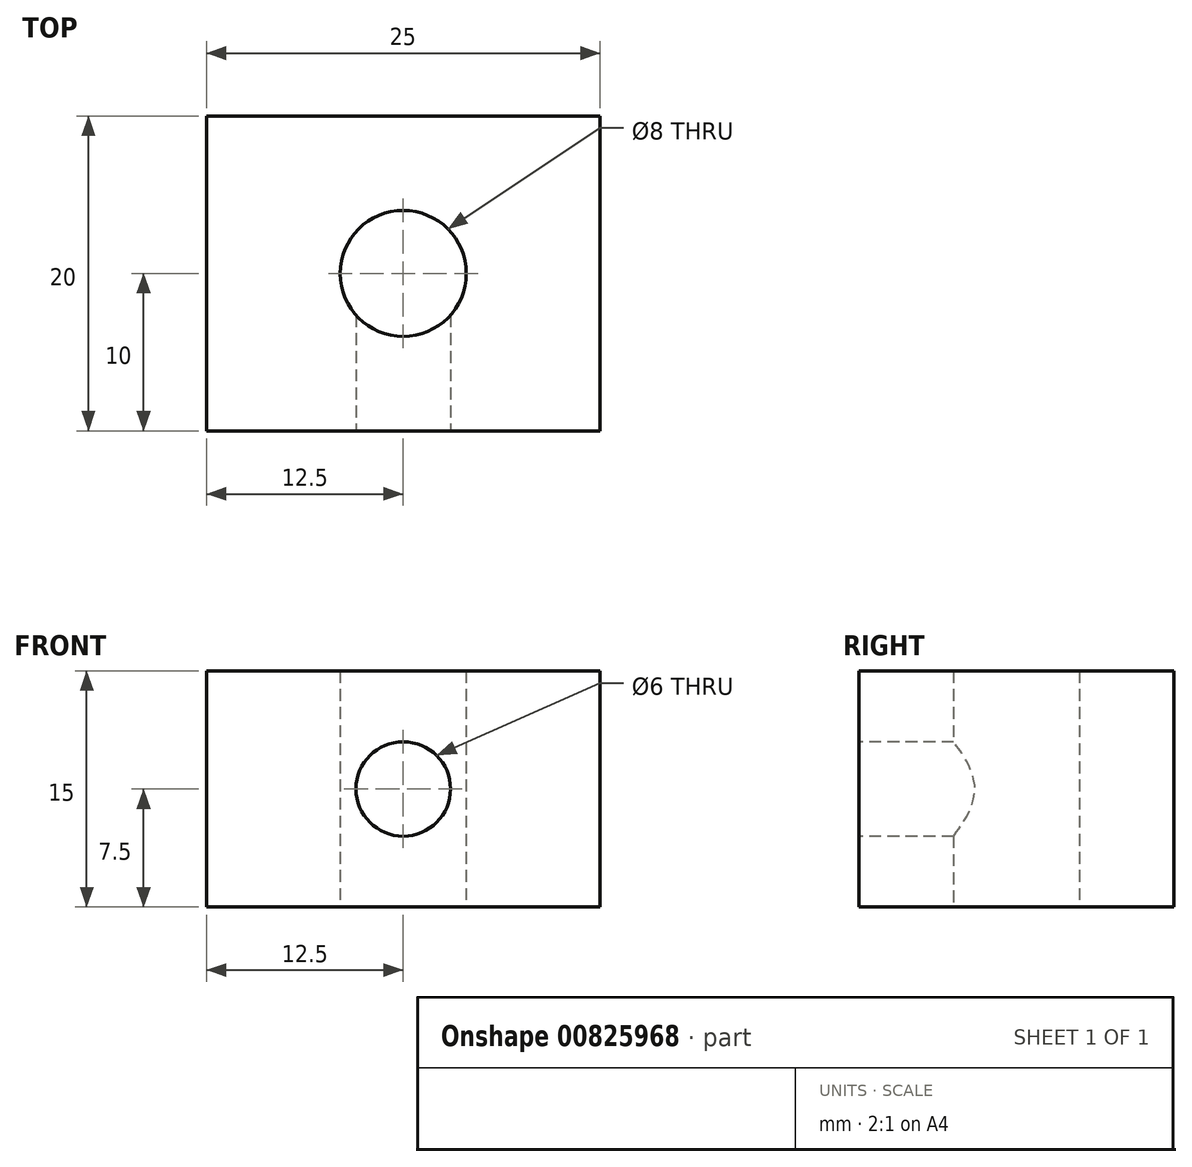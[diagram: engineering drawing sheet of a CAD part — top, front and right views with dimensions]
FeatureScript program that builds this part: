
annotation { "Feature Type Name" : "Feature", "Feature Type Description" : "" }
export const myFeature = defineFeature(function(context is Context, id is Id, definition is map)
    precondition{}
    {
        {
            var Q0;
            Q0=qCreatedBy(makeId("Top.planeOp"),FACE);
            var sketch = newSketch(context, id + "F0", { "sketchPlane" : qUnion([Q0])});
            skLineSegment(sketch, "E0.bottom", {"start": v(0, 0) * mm, "end": v(25, 0) * mm});
            skLineSegment(sketch, "E0.top", {"start": v(0, -20) * mm, "end": v(25, -20) * mm});
            skLineSegment(sketch, "E0.left", {"start": v(0, 0) * mm, "end": v(0, -20) * mm});
            skLineSegment(sketch, "E0.right", {"start": v(25, 0) * mm, "end": v(25, -20) * mm});
            skCircle(sketch, "E1", {"center": v(12.5, -10) * mm, "radius": 4 * mm});
            skLineSegment(sketch, "E2", {"start": v(0, -10) * mm, "end": v(12.5, -10) * mm, "construction": true});
            skLineSegment(sketch, "E3", {"start": v(12.5, -20) * mm, "end": v(12.5, -10) * mm, "construction": true});
            skSolve(sketch);
        }
        {
            var Q0;
            Q0=makeQuery(id+"F0.imprint","IMPRINT",FACE,{"disambiguationData":[TD([[makeQuery(id+"F0.imprint","IMPRINT",EDGE,{"derivedFrom":sQuery(id+"F0.wireOp",EDGE,"E0.bottom")}),-1.0]])]});
            extrude(context, id + "F1", {"entities" : qUnion([Q0]), "depth" : 15 * mm, "offsetDistance" : 25.4 * mm});
        }
        {
            var Q0;
            Q0=makeQuery(id+"F1.opExtrude","SWEPT_FACE",FACE,{"disambiguationData":[OSD([sQuery(id+"F0.wireOp",EDGE,"E0.top")])]});
            var sketch = newSketch(context, id + "F2", { "sketchPlane" : qUnion([Q0])});
            skCircle(sketch, "E4", {"center": v(12.5, 7.5) * mm, "radius": 3 * mm});
            skLineSegment(sketch, "E5", {"start": v(0, 7.5) * mm, "end": v(12.5, 7.5) * mm, "construction": true});
            skLineSegment(sketch, "E6", {"start": v(12.5, 0) * mm, "end": v(12.5, 7.5) * mm, "construction": true});
            skSolve(sketch);
        }
        {
            var Q0;
            Q0=makeQuery(id+"F2.imprint","IMPRINT",FACE,{"disambiguationData":[TD([[makeQuery(id+"F2.imprint","IMPRINT",EDGE,{"derivedFrom":sQuery(id+"F2.wireOp",EDGE,"E4")}),1.0]])]});
            extrude(context, id + "F3", {"entities" : qUnion([Q0]), "operationType" : NewBodyOperationType.REMOVE, "oppositeDirection" : true, "depth" : 10 * mm, "offsetDistance" : 25.4 * mm});
        }
    });
